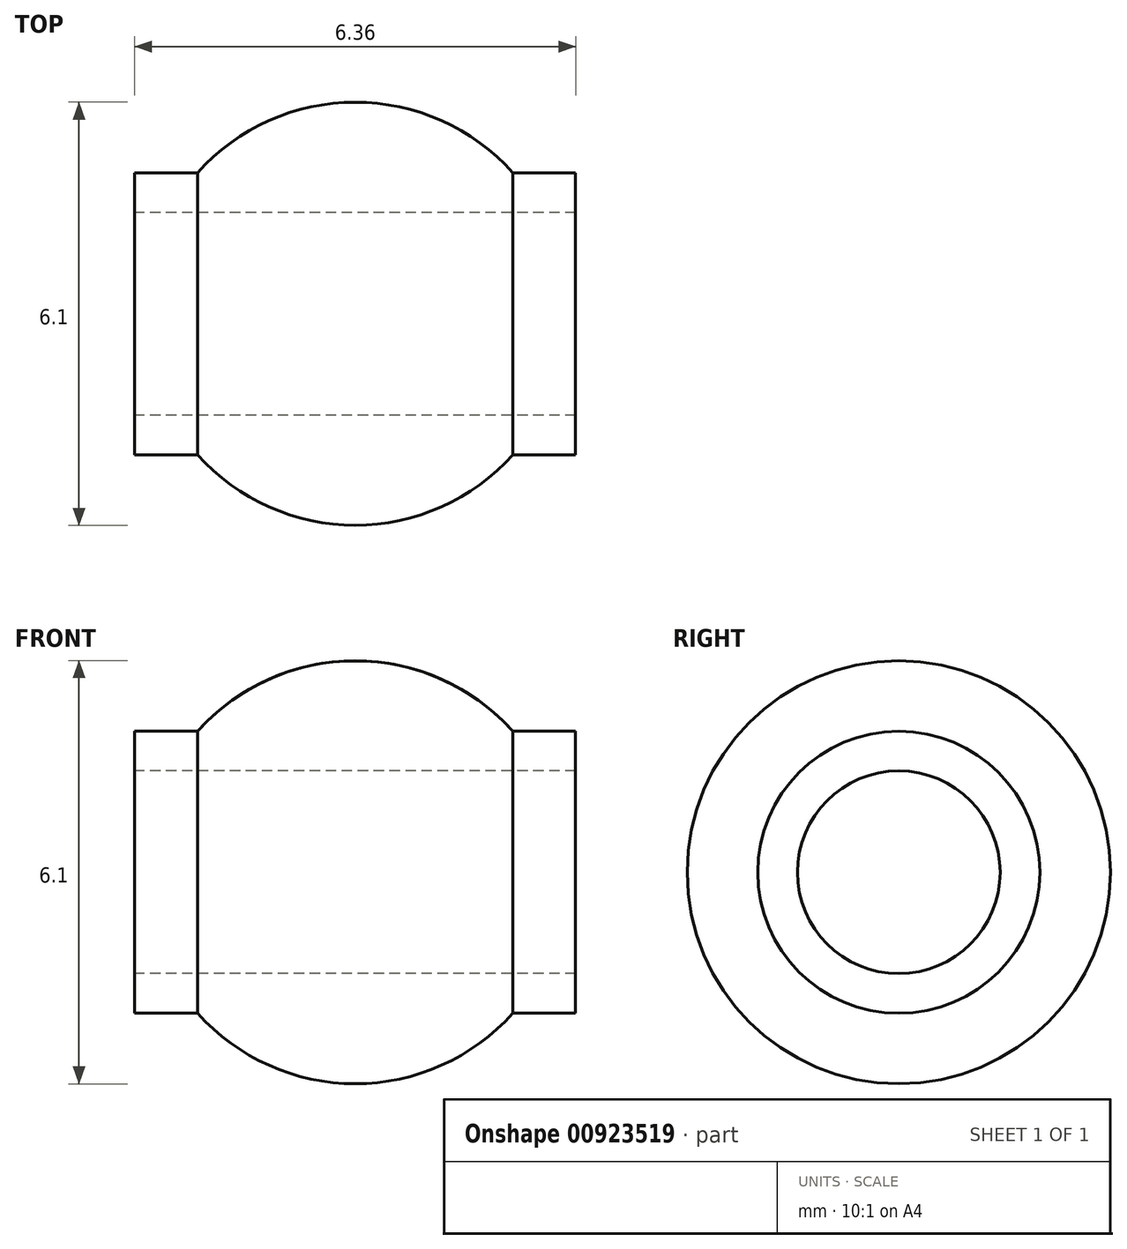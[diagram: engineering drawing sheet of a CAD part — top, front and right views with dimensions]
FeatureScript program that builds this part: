
annotation { "Feature Type Name" : "Feature", "Feature Type Description" : "" }
export const myFeature = defineFeature(function(context is Context, id is Id, definition is map)
    precondition{}
    {
        {
            var Q0;
            Q0=qCreatedBy(makeId("Front.planeOp"),FACE);
            var sketch = newSketch(context, id + "F0", { "sketchPlane" : qUnion([Q0])});
            skLineSegment(sketch, "E0", {"start": v(0, 0) * mm, "end": v(0, 38.77) * mm, "construction": true});
            skLineSegment(sketch, "E1", {"start": v(0, 0) * mm, "end": v(73.66, 0) * mm, "construction": true});
            skArc(sketch, "E2", {"start": v(2.27, 2.03) * mm, "mid": v(1.24, 2.78) * mm, "end": v(0, 3.05) * mm});
            skLineSegment(sketch, "E3", {"start": v(2.27, 2.03) * mm, "end": v(3.18, 2.03) * mm});
            skLineSegment(sketch, "E4", {"start": v(3.18, 2.03) * mm, "end": v(3.18, 1.46) * mm});
            skLineSegment(sketch, "E5", {"start": v(3.18, 1.46) * mm, "end": v(0, 1.46) * mm});
            skArc(sketch, "E6.MirrorCS", {"start": v(-2.27, 2.03) * mm, "mid": v(-1.24, 2.78) * mm, "end": v(0, 3.05) * mm});
            skLineSegment(sketch, "E7.MirrorCS", {"start": v(-2.27, 2.03) * mm, "end": v(-3.18, 2.03) * mm});
            skLineSegment(sketch, "E8.MirrorCS", {"start": v(-3.18, 2.03) * mm, "end": v(-3.18, 1.46) * mm});
            skLineSegment(sketch, "E9.MirrorCS", {"start": v(-3.18, 1.46) * mm, "end": v(0, 1.46) * mm});
            skSolve(sketch);
        }
        {
            var Q0;
            Q0 = qSketchRegion(id + "F0", true);
            var Q1;
            Q1=sQuery(id+"F0.wireOp",EDGE,"E1");
            revolve(context, id + "F1", {"surfaceOperationType" : NewSurfaceOperationType.NEW, "entities" : qUnion([Q0]), "axis" : qUnion([Q1]), "revolveType" : RevolveType.FULL});
        }
    });
